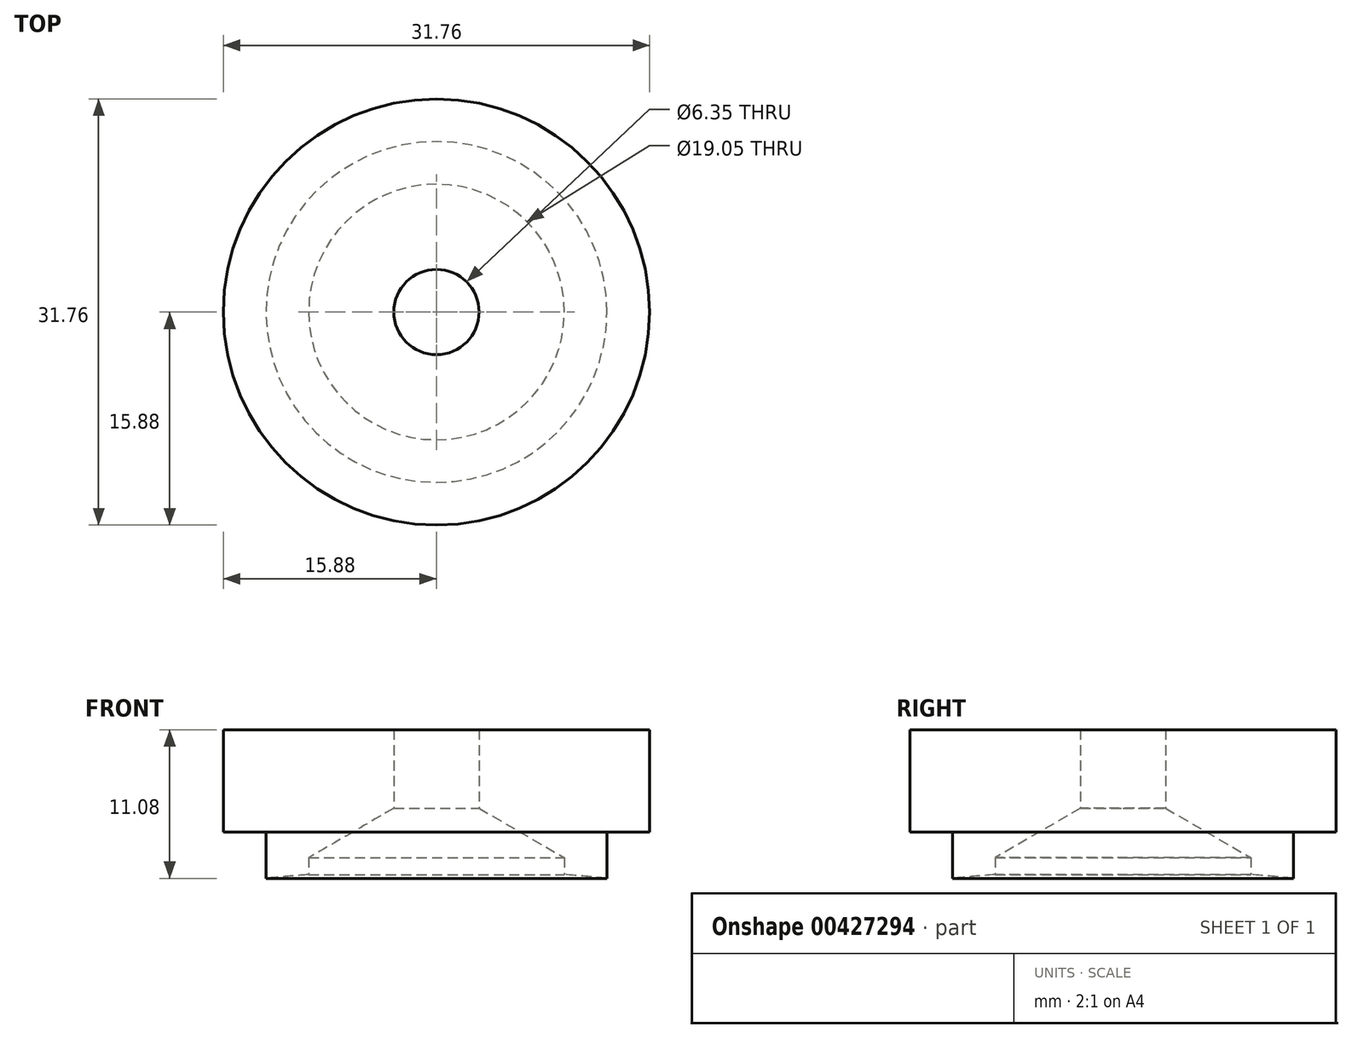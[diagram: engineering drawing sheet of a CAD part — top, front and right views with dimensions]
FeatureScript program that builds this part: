
annotation { "Feature Type Name" : "Feature", "Feature Type Description" : "" }
export const myFeature = defineFeature(function(context is Context, id is Id, definition is map)
    precondition{}
    {
        {
            var Q0;
            Q0=qCreatedBy(makeId("Front.planeOp"),FACE);
            var sketch = newSketch(context, id + "F0", { "sketchPlane" : qUnion([Q0])});
            skLineSegment(sketch, "E0", {"start": v(9.53, 1.27) * mm, "end": v(3.17, 4.94) * mm});
            skLineSegment(sketch, "E1", {"start": v(3.18, 4.94) * mm, "end": v(3.18, 10.8) * mm});
            skLineSegment(sketch, "E2", {"start": v(3.18, 10.8) * mm, "end": v(15.88, 10.8) * mm});
            skLineSegment(sketch, "E3", {"start": v(12.7, 3.18) * mm, "end": v(12.7, -0.28) * mm});
            skLineSegment(sketch, "E4", {"start": v(9.52, 1.27) * mm, "end": v(9.52, 0) * mm});
            skLineSegment(sketch, "E5", {"start": v(0, 0) * mm, "end": v(0, 20.56) * mm, "construction": true});
            skLineSegment(sketch, "E6", {"start": v(12.7, 3.18) * mm, "end": v(15.88, 3.18) * mm});
            skLineSegment(sketch, "E7", {"start": v(15.88, 3.18) * mm, "end": v(15.88, 10.8) * mm});
            skLineSegment(sketch, "E8", {"start": v(0, 0) * mm, "end": v(0, -126.64) * mm, "construction": true});
            skArc(sketch, "E9", {"start": v(12.7, -0.28) * mm, "mid": v(11.11, -0.13) * mm, "end": v(9.52, 0) * mm});
            skPoint(sketch, "E10.end.orphan", {"position": v(9.52, 0) * mm});
            skPoint(sketch, "E11.orphan", {"position": v(12.7, 0) * mm});
            skSolve(sketch);
        }
        {
            var Q0;
            Q0=makeQuery(id+"F0.imprint","IMPRINT",FACE,{"disambiguationData":[TD([[makeQuery(id+"F0.imprint","IMPRINT",EDGE,{"derivedFrom":sQuery(id+"F0.wireOp",EDGE,"E0")}),-1.0]])]});
            var Q1;
            Q1=sQuery(id+"F0.wireOp",EDGE,"E5");
            revolve(context, id + "F1", {"entities" : qUnion([Q0]), "axis" : qUnion([Q1]), "revolveType" : RevolveType.FULL});
        }
    });
